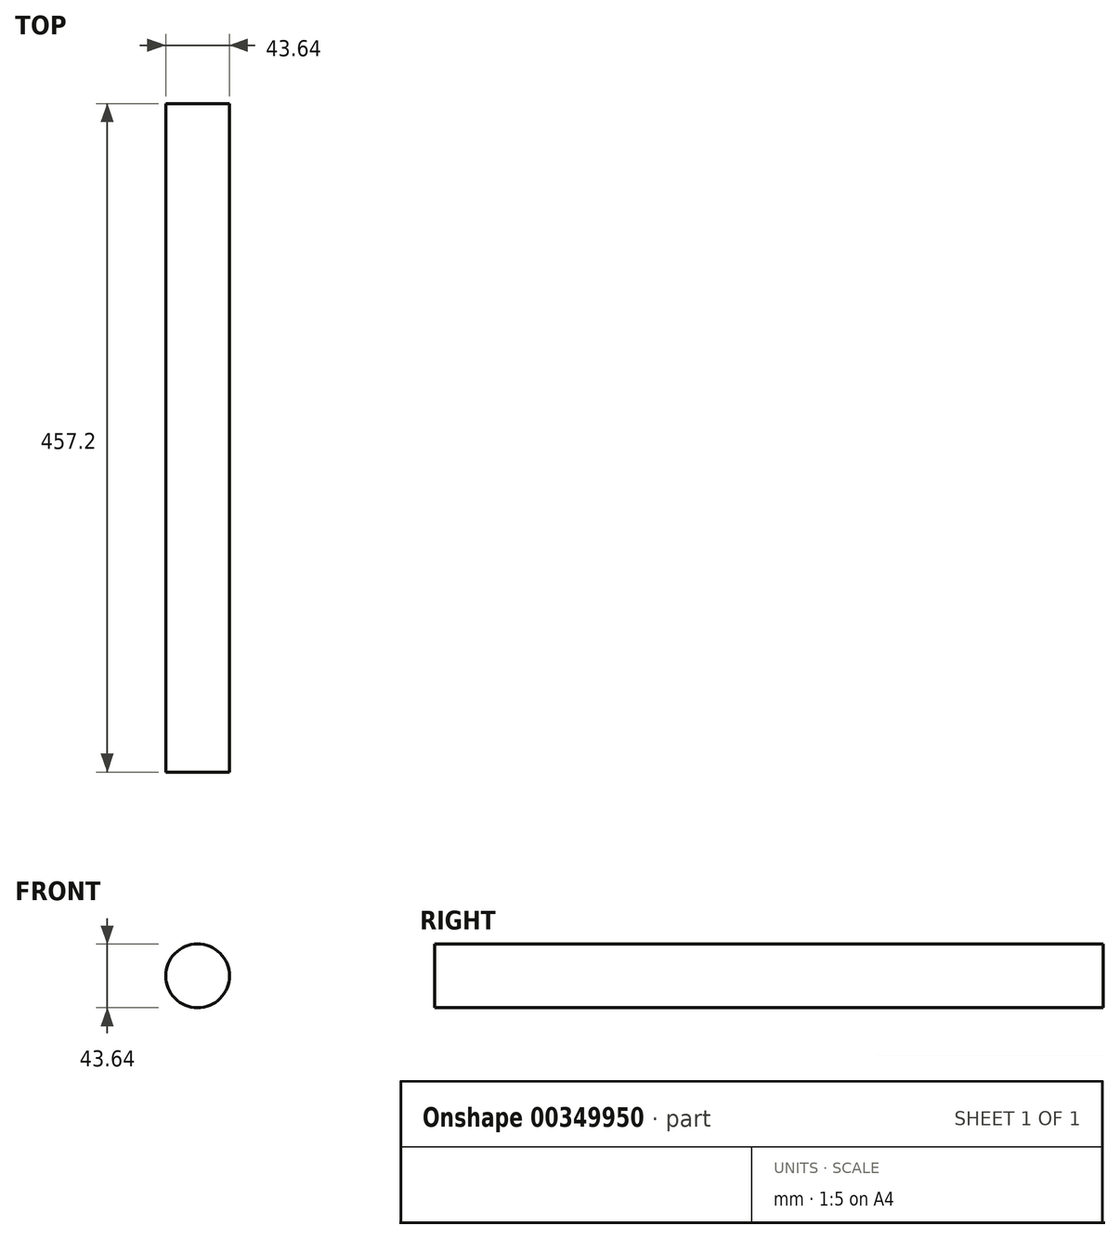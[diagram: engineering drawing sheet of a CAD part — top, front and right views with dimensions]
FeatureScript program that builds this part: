
annotation { "Feature Type Name" : "Feature", "Feature Type Description" : "" }
export const myFeature = defineFeature(function(context is Context, id is Id, definition is map)
    precondition{}
    {
        {
            var Q0;
            Q0=qCreatedBy(makeId("Front.planeOp"),FACE);
            var sketch = newSketch(context, id + "F0", { "sketchPlane" : qUnion([Q0])});
            skCircle(sketch, "E0", {"center": v(0, 0) * mm, "radius": 21.82 * mm});
            skSolve(sketch);
        }
        {
            var Q0;
            Q0 = qSketchRegion(id + "F0", true);
            extrude(context, id + "F1", {"entities" : qUnion([Q0]), "depth" : 457.2 * mm, "offsetDistance" : 25.4 * mm});
        }
    });
